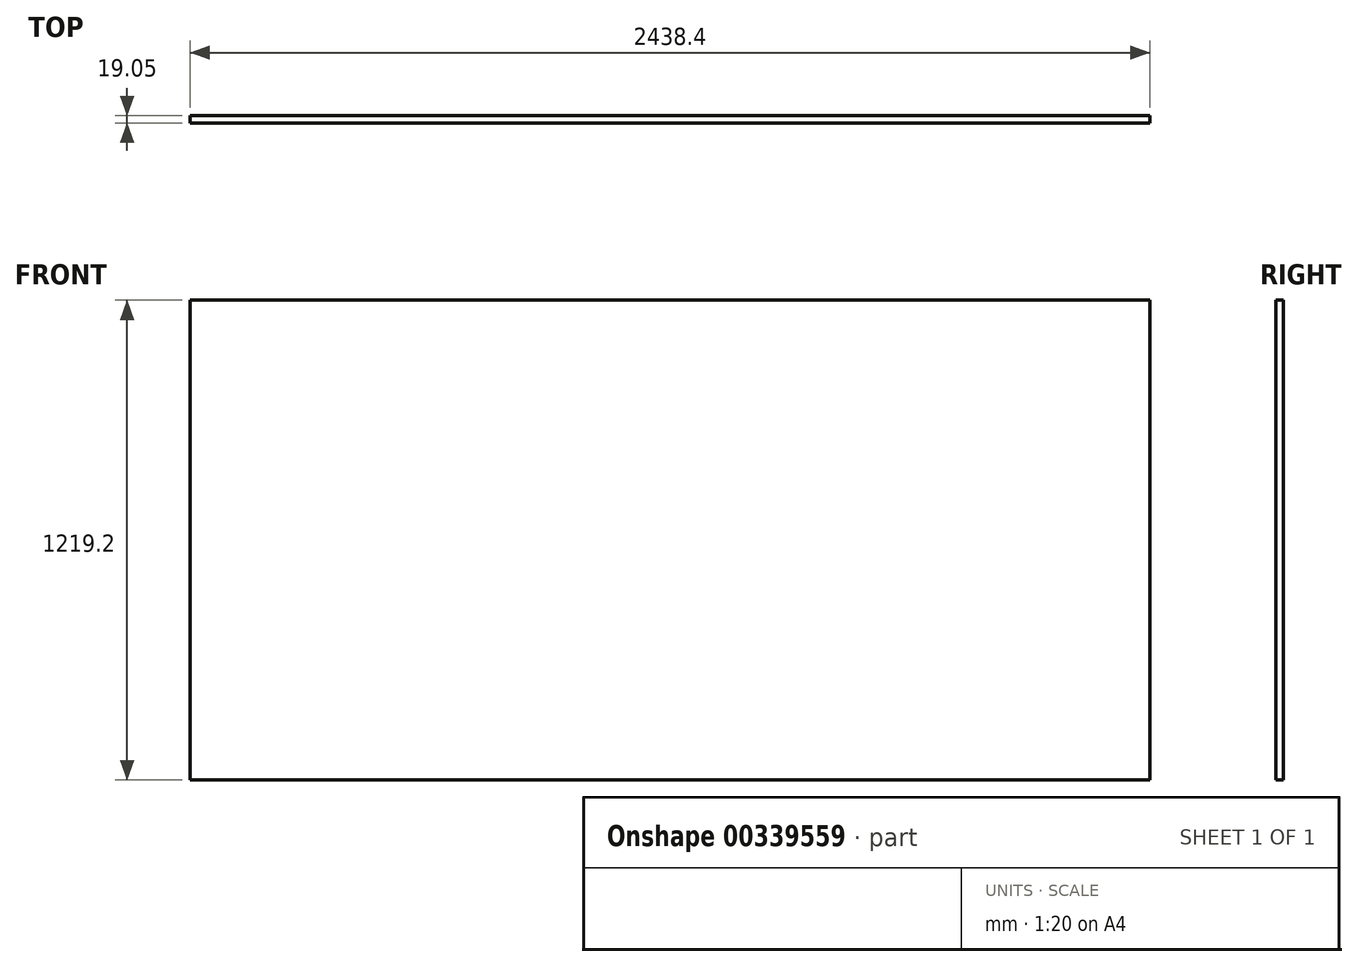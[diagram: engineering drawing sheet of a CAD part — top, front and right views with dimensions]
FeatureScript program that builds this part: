
annotation { "Feature Type Name" : "Feature", "Feature Type Description" : "" }
export const myFeature = defineFeature(function(context is Context, id is Id, definition is map)
    precondition{}
    {
        {
            var Q0;
            Q0=qCreatedBy(makeId("Front.planeOp"),FACE);
            var sketch = newSketch(context, id + "F0", { "sketchPlane" : qUnion([Q0])});
            skLineSegment(sketch, "E0.bottom", {"start": v(-2353.97, 1193.96) * mm, "end": v(84.43, 1193.96) * mm});
            skLineSegment(sketch, "E0.top", {"start": v(-2353.97, -25.24) * mm, "end": v(84.43, -25.24) * mm});
            skLineSegment(sketch, "E0.left", {"start": v(-2353.97, 1193.96) * mm, "end": v(-2353.97, -25.24) * mm});
            skLineSegment(sketch, "E0.right", {"start": v(84.43, 1193.96) * mm, "end": v(84.43, -25.24) * mm});
            skSolve(sketch);
        }
        {
            var Q0;
            Q0 = qSketchRegion(id + "F0", true);
            extrude(context, id + "F1", {"entities" : qUnion([Q0]), "depth" : 19.05 * mm});
        }
    });
